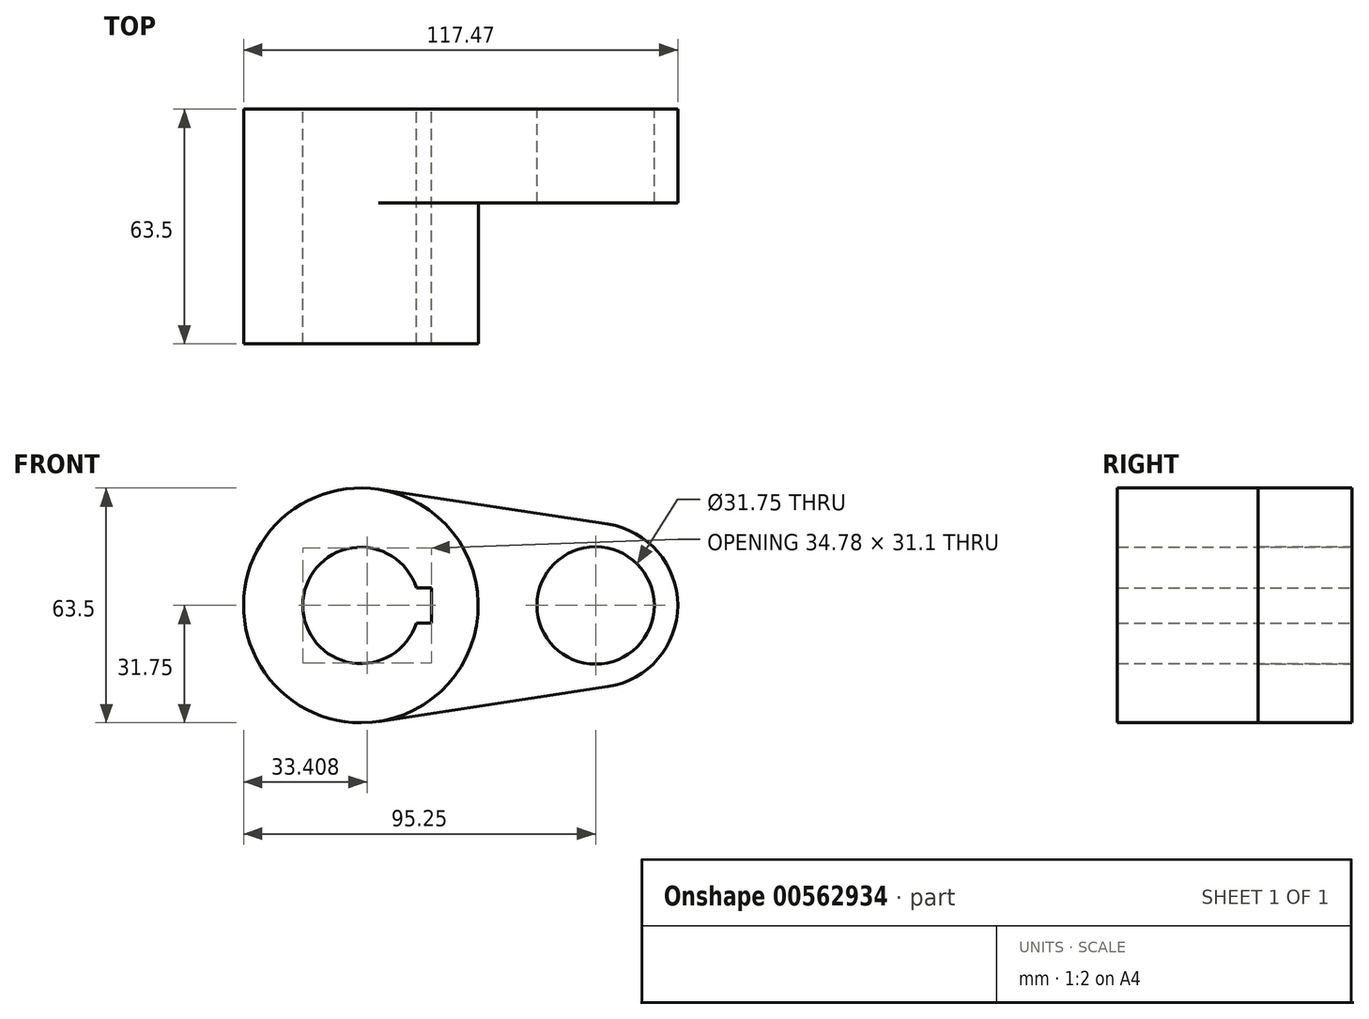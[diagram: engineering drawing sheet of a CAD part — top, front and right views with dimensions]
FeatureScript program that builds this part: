
annotation { "Feature Type Name" : "Feature", "Feature Type Description" : "" }
export const myFeature = defineFeature(function(context is Context, id is Id, definition is map)
    precondition{}
    {
        {
            var Q0;
            Q0=qCreatedBy(makeId("Front.planeOp"),FACE);
            var sketch = newSketch(context, id + "F0", { "sketchPlane" : qUnion([Q0])});
            skCircle(sketch, "E0", {"center": v(0, 0) * mm, "radius": 31.75 * mm});
            skCircle(sketch, "E1", {"center": v(63.5, 0) * mm, "radius": 22.23 * mm});
            skLineSegment(sketch, "E2", {"start": v(4.76, 31.4) * mm, "end": v(66.83, 21.97) * mm});
            skLineSegment(sketch, "E3", {"start": v(4.76, -31.4) * mm, "end": v(66.83, -21.97) * mm});
            skCircle(sketch, "E4", {"center": v(0, 0) * mm, "radius": 15.73 * mm});
            skCircle(sketch, "E5", {"center": v(63.5, 0) * mm, "radius": 15.88 * mm});
            skLineSegment(sketch, "E6.bottom", {"start": v(-19.05, 4.76) * mm, "end": v(19.05, 4.76) * mm});
            skLineSegment(sketch, "E6.top", {"start": v(-19.05, -4.76) * mm, "end": v(19.05, -4.76) * mm});
            skLineSegment(sketch, "E6.left", {"start": v(-19.05, 4.76) * mm, "end": v(-19.05, -4.76) * mm});
            skLineSegment(sketch, "E6.right", {"start": v(19.05, 4.76) * mm, "end": v(19.05, -4.76) * mm});
            skSolve(sketch);
        }
        {
            var Q0;
            {var subQ5=sQuery(id+"F0.wireOp",EDGE,"E6.left");Q0=makeQuery(id+"F0.imprint","IMPRINT",FACE,{"disambiguationData":[TD([[makeQuery(id+"F0.imprint","IMPRINT",EDGE,{"derivedFrom":subQ5}),1.0]])]});}
            var Q1;
            {var subQ7=sQuery(id+"F0.wireOp",EDGE,"E6.left");Q1=makeQuery(id+"F0.imprint","IMPRINT",FACE,{"disambiguationData":[TD([[makeQuery(id+"F0.imprint","IMPRINT",EDGE,{"derivedFrom":subQ7}),-1.0]])]});}
            var Q2;
            Q2=makeQuery(id+"F0.imprint","IMPRINT",FACE,{"disambiguationData":[TD([[makeQuery(id+"F0.imprint","IMPRINT",EDGE,{"derivedFrom":sQuery(id+"F0.wireOp",EDGE,"E5")}),-1.0]])]});
            var Q3;
            {var subQ0=sQuery(id+"F0.wireOp",EDGE,"E2");Q3=makeQuery(id+"F0.imprint","IMPRINT",FACE,{"disambiguationData":[TD([[makeQuery(id+"F0.imprint","IMPRINT",EDGE,{"derivedFrom":subQ0}),-1.0]])]});}
            extrude(context, id + "F1", {"entities" : qUnion([Q0, Q1, Q2, Q3]), "depth" : 25.4 * mm, "offsetDistance" : 25.4 * mm});
        }
        {
            var Q0;
            {var subQ7=sQuery(id+"F0.wireOp",EDGE,"E6.left");Q0=makeQuery(id+"F0.imprint","IMPRINT",FACE,{"disambiguationData":[TD([[makeQuery(id+"F0.imprint","IMPRINT",EDGE,{"derivedFrom":subQ7}),-1.0]])]});}
            var Q1;
            {var subQ5=sQuery(id+"F0.wireOp",EDGE,"E6.left");Q1=makeQuery(id+"F0.imprint","IMPRINT",FACE,{"disambiguationData":[TD([[makeQuery(id+"F0.imprint","IMPRINT",EDGE,{"derivedFrom":subQ5}),1.0]])]});}
            extrude(context, id + "F2", {"entities" : qUnion([Q0, Q1]), "operationType" : NewBodyOperationType.ADD, "depth" : 63.5 * mm, "offsetDistance" : 25.4 * mm});
        }
    });
